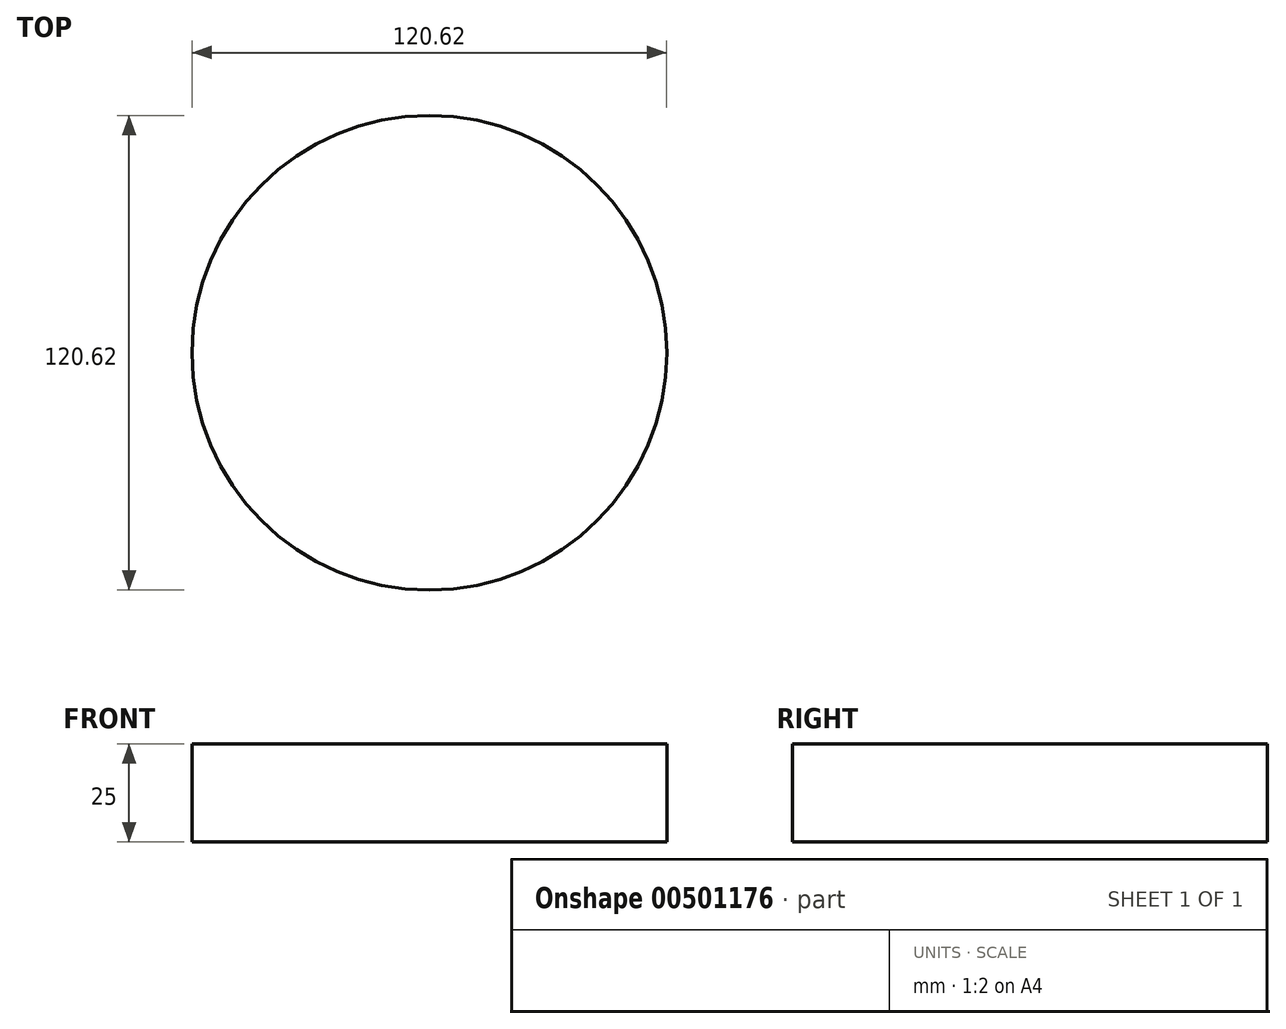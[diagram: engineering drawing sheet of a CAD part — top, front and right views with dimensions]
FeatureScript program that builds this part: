
annotation { "Feature Type Name" : "Feature", "Feature Type Description" : "" }
export const myFeature = defineFeature(function(context is Context, id is Id, definition is map)
    precondition{}
    {
        {
            var Q0;
            Q0=qCreatedBy(makeId("Top.planeOp"),FACE);
            var sketch = newSketch(context, id + "F0", { "sketchPlane" : qUnion([Q0])});
            skCircle(sketch, "E0", {"center": v(0, 0) * mm, "radius": 60.31 * mm});
            skSolve(sketch);
        }
        {
            var Q0;
            Q0=makeQuery(id+"F0.imprint","IMPRINT",FACE,{"disambiguationData":[TD([[makeQuery(id+"F0.imprint","IMPRINT",EDGE,{"derivedFrom":sQuery(id+"F0.wireOp",EDGE,"E0")}),1.0]])]});
            extrude(context, id + "F1", {"entities" : qUnion([Q0]), "depth" : 25 * mm});
        }
    });
